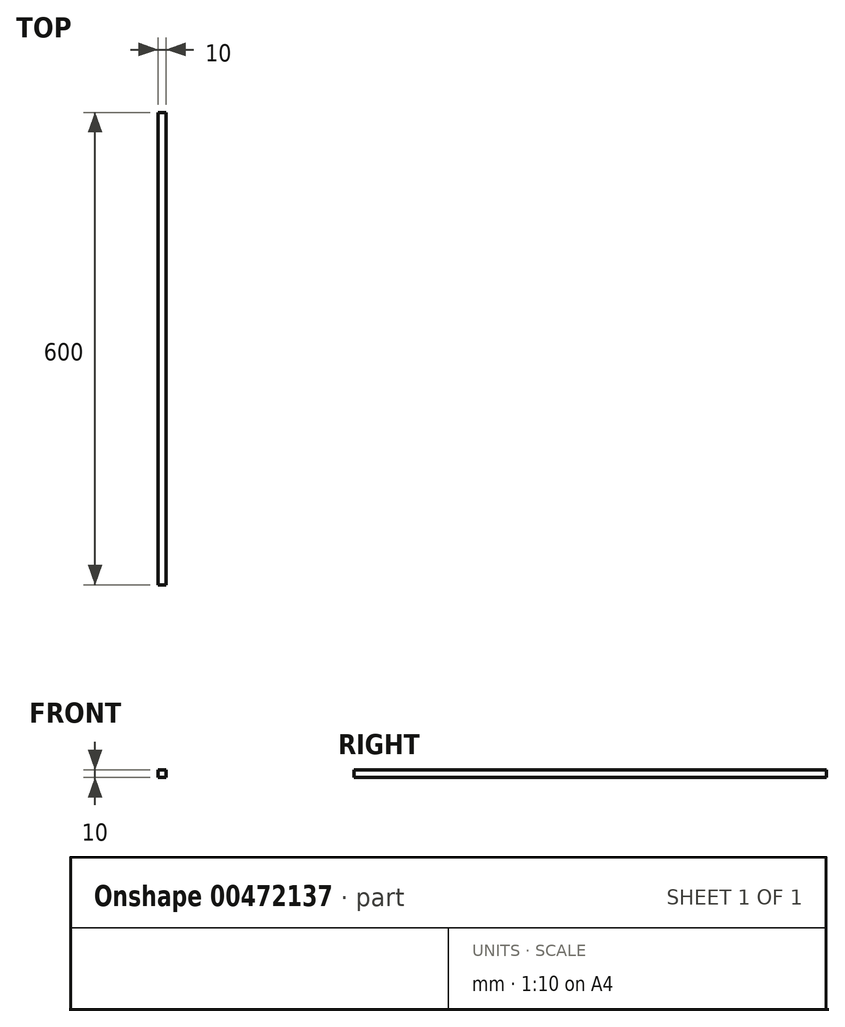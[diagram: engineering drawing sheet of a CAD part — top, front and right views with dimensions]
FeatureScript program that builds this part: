
annotation { "Feature Type Name" : "Feature", "Feature Type Description" : "" }
export const myFeature = defineFeature(function(context is Context, id is Id, definition is map)
    precondition{}
    {
        {
            var Q0;
            Q0=qCreatedBy(makeId("Front.planeOp"),FACE);
            var sketch = newSketch(context, id + "F0", { "sketchPlane" : qUnion([Q0])});
            skLineSegment(sketch, "E0.bottom", {"start": v(5, -5) * mm, "end": v(-5, -5) * mm});
            skLineSegment(sketch, "E0.top", {"start": v(5, 5) * mm, "end": v(-5, 5) * mm});
            skLineSegment(sketch, "E0.left", {"start": v(5, -5) * mm, "end": v(5, 5) * mm});
            skLineSegment(sketch, "E0.right", {"start": v(-5, -5) * mm, "end": v(-5, 5) * mm});
            skPoint(sketch, "E0.middle", {"position": v(0, 0) * mm});
            skSolve(sketch);
        }
        {
            var Q0;
            Q0=makeQuery(id+"F0.imprint","IMPRINT",FACE,{"disambiguationData":[TD([[makeQuery(id+"F0.imprint","IMPRINT",EDGE,{"derivedFrom":sQuery(id+"F0.wireOp",EDGE,"E0.bottom")}),-1.0]])]});
            extrude(context, id + "F1", {"entities" : qUnion([Q0]), "depth" : 600 * mm});
        }
        {
            var Q0;
            Q0=makeQuery(id+"F1.opExtrude","SWEPT_FACE",FACE,{"disambiguationData":[OSD([sQuery(id+"F0.wireOp",EDGE,"E0.bottom")])]});
            var sketch = newSketch(context, id + "F2", { "sketchPlane" : qUnion([Q0])});
            skLineSegment(sketch, "E1", {"start": v(5, 585) * mm, "end": v(-5, 585) * mm, "construction": true});
            skPoint(sketch, "E2", {"position": v(0, 585) * mm});
            skLineSegment(sketch, "E3", {"start": v(5, 395) * mm, "end": v(-5, 395) * mm, "construction": true});
            skLineSegment(sketch, "E4", {"start": v(5, 205) * mm, "end": v(-5, 205) * mm, "construction": true});
            skLineSegment(sketch, "E5", {"start": v(5, 15) * mm, "end": v(-5, 15) * mm, "construction": true});
            skPoint(sketch, "E6", {"position": v(0, 395) * mm});
            skPoint(sketch, "E7", {"position": v(0, 205) * mm});
            skPoint(sketch, "E8", {"position": v(-17.68, 101.52) * mm});
            skPoint(sketch, "E9", {"position": v(0, 15) * mm});
            skSolve(sketch);
        }
    });
